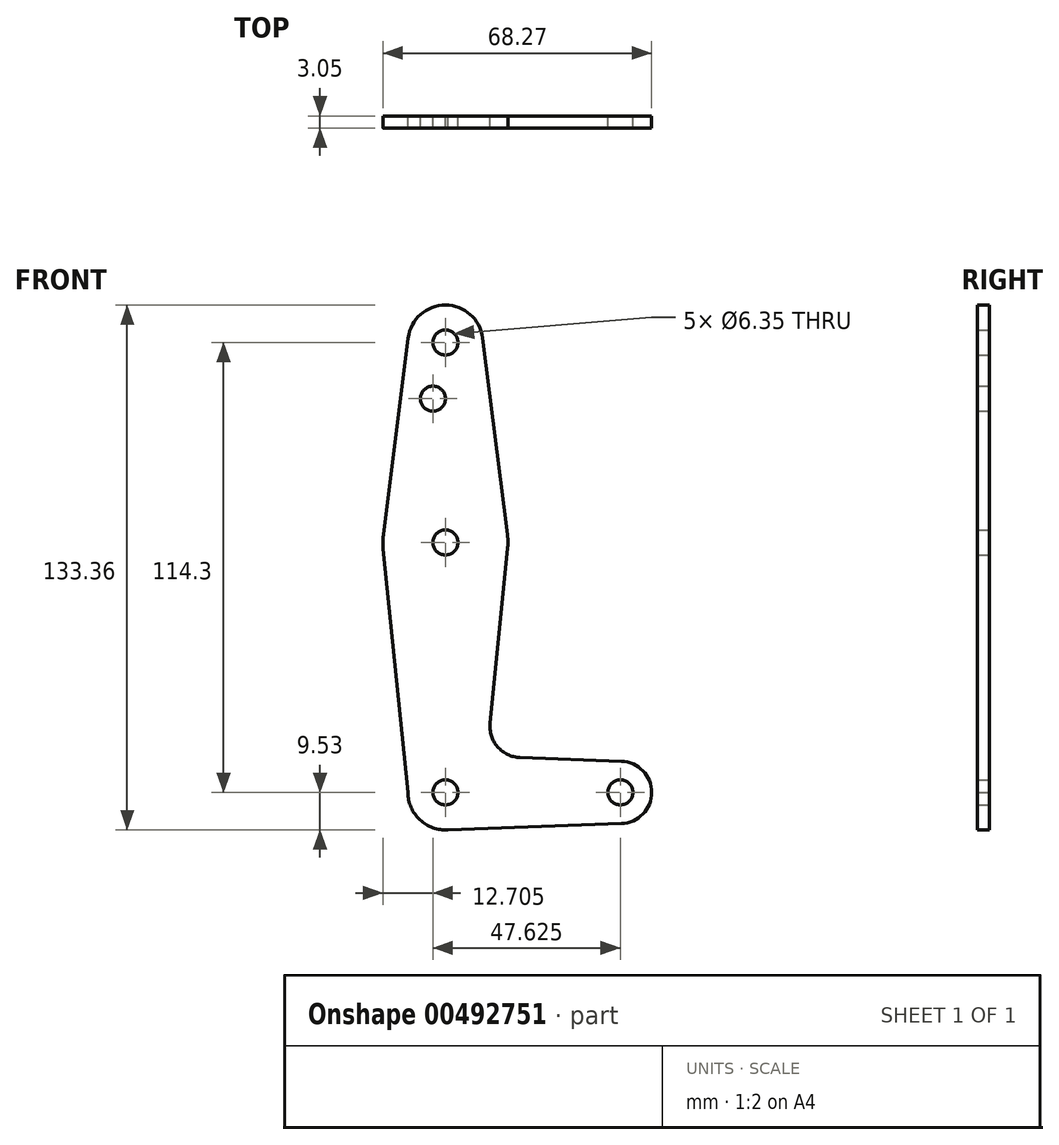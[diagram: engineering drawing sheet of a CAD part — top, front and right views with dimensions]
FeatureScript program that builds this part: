
annotation { "Feature Type Name" : "Feature", "Feature Type Description" : "" }
export const myFeature = defineFeature(function(context is Context, id is Id, definition is map)
    precondition{}
    {
        {
            var Q0;
            Q0=qCreatedBy(makeId("Front.planeOp"),FACE);
            var sketch = newSketch(context, id + "F0", { "sketchPlane" : qUnion([Q0])});
            skLineSegment(sketch, "E0", {"start": v(0, 0) * mm, "end": v(0, 114.3) * mm, "construction": true});
            skCircle(sketch, "E1", {"center": v(0, 114.3) * mm, "radius": 9.53 * mm});
            skCircle(sketch, "E2", {"center": v(0, 63.5) * mm, "radius": 15.88 * mm});
            skCircle(sketch, "E3", {"center": v(0, 0) * mm, "radius": 9.53 * mm});
            skLineSegment(sketch, "E4", {"start": v(0, 0) * mm, "end": v(44.45, 0) * mm, "construction": true});
            skCircle(sketch, "E5", {"center": v(44.45, 0) * mm, "radius": 7.94 * mm});
            skLineSegment(sketch, "E6", {"start": v(-9.45, 115.5) * mm, "end": v(-15.75, 65.48) * mm});
            skLineSegment(sketch, "E7", {"start": v(9.45, 115.5) * mm, "end": v(15.75, 65.48) * mm});
            skLineSegment(sketch, "E8", {"start": v(18.97, 8.85) * mm, "end": v(44.73, 7.93) * mm});
            skLineSegment(sketch, "E9", {"start": v(0, -9.53) * mm, "end": v(44.73, -7.93) * mm});
            skLineSegment(sketch, "E10", {"start": v(-9.53, 0) * mm, "end": v(-15.8, 61.9) * mm});
            skLineSegment(sketch, "E11", {"start": v(11.34, 17.6) * mm, "end": v(15.8, 61.91) * mm});
            skCircle(sketch, "E12", {"center": v(0, 114.3) * mm, "radius": 3.18 * mm});
            skCircle(sketch, "E13", {"center": v(0, 63.5) * mm, "radius": 3.18 * mm});
            skCircle(sketch, "E14", {"center": v(0, 0) * mm, "radius": 3.18 * mm});
            skCircle(sketch, "E15", {"center": v(44.45, 0) * mm, "radius": 3.18 * mm});
            skCircle(sketch, "E16", {"center": v(-3.18, 100.03) * mm, "radius": 3.18 * mm});
            skArc(sketch, "E17.filletArc", {"start": v(11.34, 17.6) * mm, "mid": v(13.26, 11.57) * mm, "end": v(18.97, 8.85) * mm});
            skSolve(sketch);
        }
        {
            var Q0;
            Q0 = qSketchRegion(id + "F0", true);
            extrude(context, id + "F1", {"entities" : qUnion([Q0]), "depth" : 3.05 * mm});
        }
    });
